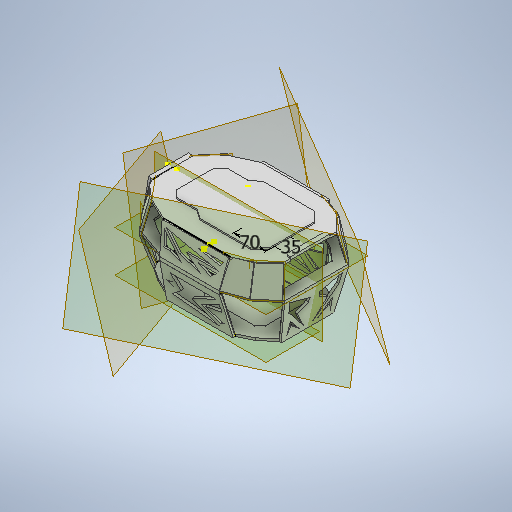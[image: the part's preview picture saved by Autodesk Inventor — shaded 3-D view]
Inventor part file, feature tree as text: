
AUTODESK INVENTOR PART (.ipt)
format: ipt  version: 2025.2 (Build 292293000, 293)  size: 6,125,568 bytes
history: native  units: mm
features: sketch x47, extrude x37, other x23, plane x17, loft x11, mirror x2, chamfer x2
ambient origin geometry x8: Origin, YZ Plane, XZ Plane, XY Plane, X Axis, Y Axis, Z Axis, Center Point
bodies: Body1 (feature_tree)
feature tree (139):
  extrude  "Extrusion2"  Depth=45.0mm
  extrude  "Extrusion3"  Depth=40.0mm
  plane  "Work Plane3"
  extrude  "Extrusion4"  Depth=145.0mm
  extrude  "Extrusion5"  Depth=55.0mm
  plane  "Work Plane4"
  extrude  "Extrusion6"  Depth=40.0mm
  sketch  "Sketch8"  dims[d17=165.0deg d18=15.0mm]
  sketch  "Sketch9"  dims[d20=10.0mm d21=40.0mm]
  sketch  "Sketch10"  dims[d22=5.0mm d23=5.0mm]
  loft  "Loft1"
  loft  "Loft2"
  extrude  "Extrusion7"  Depth=5.0mm
  extrude  "Extrusion8"  TaperAngle=90.0deg  [1 undecoded]
  extrude  "Extrusion9"  Depth=30.0mm
  sketch  "Sketch14"  dims[d30=45.0mm d31=20.0mm]
  sketch  "Sketch15"  dims[d32=45.0deg d39=5.0mm d40=0.0mm]
  sketch  "Sketch16"  dims[d41=3.0mm d42=3.0mm d43=0.0mm d44=0.0mm d45=150.0mm]
  loft  "Loft3"
  loft  "Loft4"
  loft  "Loft5"
  extrude  "Extrusion10"  Depth=150.0mm
  extrude  "Extrusion11"  Depth=10.0mm
  extrude  "Extrusion12"  Depth=10.0mm
  extrude  "Extrusion13"  Depth=10.0mm
  extrude  "Extrusion14"  Depth=10.0mm
  loft  "Loft7"
  loft  "Loft8"
  sketch  "Sketch22"  dims[d57=10.0mm d58=10.0mm]
  plane  "Work Plane5"
  extrude  "Extrusion15"  Depth=3.0mm TaperAngle=0.0deg
  plane  "Work Plane6"
  extrude  "Extrusion16"  Depth=10.0mm
  extrude  "Extrusion17"  Depth=50.0mm
  plane  "Work Plane7"
  extrude  "Extrusion18"  Depth=50.0mm
  sketch  "Sketch28"  dims[d71=27.925268mm d72=10.0mm]
  extrude  "Extrusion19"  Depth=10.0mm
  extrude  "Extrusion20"  Depth=60.0mm
  extrude  "Extrusion21"  Depth=5.0mm TaperAngle=0.0deg
  extrude  "Extrusion22"  TaperAngle=0.0deg  [1 undecoded]
  extrude  "Extrusion23"  TaperAngle=0.0deg  [1 undecoded]
  extrude  "Extrusion24"  Depth=4.0mm TaperAngle=0.0deg
  extrude  "Extrusion25"  TaperAngle=0.0deg  [1 undecoded]
  extrude  "Extrusion26"  TaperAngle=0.0deg  [1 undecoded]
  extrude  "Extrusion27"  TaperAngle=0.0deg  [1 undecoded]
  plane  "Work Plane8"
  mirror  "Mirror1"
  loft  "Loft9"
  loft  "Loft10"
  loft  "Loft11"
  loft  "Loft12"
  plane  "Work Plane14"
  plane  "Work Plane15"
  extrude  "Extrusion28"  TaperAngle=0.0deg  [1 undecoded]
  extrude  "Extrusion29"  Depth=4.0mm TaperAngle=0.0deg
  plane  "Work Plane16"
  extrude  "Extrusion30"  Depth=4.0mm
  mirror  "Mirror2"
  extrude  "Extrusion31"  Depth=70.0mm
  sketch  "Sketch42"  dims[d126=4.0mm d127=0.0mm d128=4.0mm d129=0.0mm]
  extrude  "Extrusion32"  Depth=10.0mm
  extrude  "Extrusion33"  Depth=70.0mm
  extrude  "Extrusion34"  Depth=35.0mm
  extrude  "Extrusion35"  Depth=23.0mm TaperAngle=0.0deg
  chamfer  "Chamfer1"  Distance=17.5mm
  extrude  "Extrusion36"  Depth=25.0mm
  chamfer  "Chamfer2"  Distance=30.0mm
  sketch  "Sketch48"  dims[d142=90.0deg d143=23.0mm d144=0.0mm]
  extrude  "Extrusion37"  TaperAngle=15.0deg  [1 undecoded]
  extrude  "Extrusion38"  TaperAngle=90.0deg  [1 undecoded]
  sketch  "Sketch1"  dims[d6=115.0mm d8=45.0mm]
  other  "Image1"
  sketch  "Sketch3"  dims[d9=45.0deg d10=40.0mm]
  sketch  "Sketch4"  dims[d11=27.925268mm d12=145.0mm]
  sketch  "Sketch5"  dims[d13=27.052603mm d14=55.0mm]
  sketch  "Sketch6"  dims[d15=27.052603mm d16=40.0mm]
  other  "Edges1"
  other  "Edges2"
  other  "Edges3"
  other  "Edges4"
  sketch  "Sketch11"  dims[d24=40.0mm d25=90.0deg]
  sketch  "Sketch12"  dims[d26=30.0mm d27=110.0mm]
  sketch  "Sketch13"  dims[d28=25.0mm d29=25.307274mm]
  other  "Edges5"
  other  "Edges6"
  other  "Edges7"
  other  "Edges8"
  other  "Edges9"
  other  "Edges10"
  sketch  "Sketch17"  dims[d46=10.0mm d48=10.0mm]
  sketch  "Sketch18"  dims[d49=10.0mm d50=22.68928mm]
  sketch  "Sketch19"  dims[d51=10.0mm d52=10.0mm]
  sketch  "Sketch20"  dims[d53=10.0mm d54=10.0mm]
  sketch  "Sketch21"  dims[d55=10.0mm d56=10.0mm]
  other  "Edges13"
  other  "Edges14"
  other  "Edges15"
  other  "Edges16"
  sketch  "Sketch23"  dims[d59=5.0mm d60=0.0mm d61=3.0mm d62=3.0mm d63=0.0mm d64=0.0mm]
  sketch  "Sketch24"  dims[d65=-90.0mm d66=10.0mm]
  sketch  "Sketch25"  dims[d67=70.0mm d68=50.0mm]
  sketch  "Sketch26"  dims[d69=22.68928mm d70=50.0mm]
  sketch  "Sketch29"  dims[d73=50.0mm d74=60.0mm]
  sketch  "Sketch30"  dims[d75=70.0mm d76=5.0mm d77=0.0mm]
  sketch  "Sketch31"  dims[d78=0.0mm d79=90.0deg d80=0.0mm d81=90.0deg]
  sketch  "Sketch32"  dims[d82=0.0mm d83=90.0deg d84=0.0mm d85=90.0deg]
  sketch  "Sketch33"  dims[d86=4.0mm d87=0.0mm d88=4.0mm d89=0.0mm]
  sketch  "Sketch34"  dims[d90=4.0mm d91=0.0mm d92=0.0mm d93=90.0deg]
  sketch  "Sketch35"  dims[d94=0.0mm d95=90.0deg d96=0.0mm d97=90.0deg]
  sketch  "Sketch36"  dims[d98=0.0mm d99=90.0deg d100=0.0mm d101=90.0deg]
  sketch  "Sketch37"  dims[d102=0.0mm d103=90.0deg d104=4.0mm d105=0.0mm]
  plane  "Work Plane9"
  plane  "Work Plane10"
  plane  "Work Plane11"
  plane  "Work Plane12"
  plane  "Work Plane13"
  other  "Edges17"
  other  "Edges18"
  other  "Edges19"
  other  "Edges20"
  other  "Edges21"
  other  "Edges22"
  other  "Edges23"
  other  "Edges24"
  sketch  "Sketch38"  dims[d106=4.0mm d107=0.0mm d108=4.0mm d109=0.0mm]
  sketch  "Sketch39"  dims[d110=4.0mm d111=0.0mm d112=4.0mm d113=0.0mm]
  sketch  "Sketch40"  dims[d118=0.0mm d119=90.0deg d120=0.0mm d121=90.0deg]
  plane  "Work Plane17"
  plane  "Work Plane18"
  plane  "Work Plane19"
  sketch  "Sketch41"  dims[d122=0.0mm d123=90.0deg d124=0.0mm d125=90.0deg]
  sketch  "Sketch43"  dims[d130=4.0mm d131=0.0mm d132=92.689mm]
  sketch  "Sketch44"  dims[d133=4.0mm d134=0.0mm d135=70.0mm]
  sketch  "Sketch45"  dims[d136=35.0mm d137=10.0mm]
  sketch  "Sketch46"  dims[d138=50.0mm d139=70.0mm]
  sketch  "Sketch47"  dims[d140=50.0mm d141=35.0mm]
  sketch  "Sketch49"  dims[d145=70.0mm]
  sketch  "Sketch50"  dims[d146=3.0mm d147=17.5mm d148=0.0mm d149=25.0mm d150=30.0mm d151=15.0deg d152=90.0deg d153=5.0mm d154=20.0mm d155=90.0deg d156=4.363323mm d157=17.5mm d158=0.0mm d159=25.0mm d160=165.0deg d161=40.0mm d162=150.0deg d163=50.0mm d164=1.745329mm d165=40.0mm d166=5.0mm d167=40.0mm d168=30.543262mm d169=17.5mm d170=0.0mm d171=10.0mm d172=100.0mm d173=150.0deg d174=40.0mm d175=19.198622mm d176=100.0mm d177=70.0mm d178=30.0deg d179=100.0mm d180=10.0mm d181=10.0mm d182=10.0mm d183=4.363323mm d184=40.0mm d185=40.0mm d186=6.981317mm d187=20.0mm d188=24.43461mm d189=16.0mm d190=10.0mm d191=0.0mm d192=80.0mm d193=24.43461mm d194=120.0mm d195=30.0deg d196=40.0mm d197=30.0deg d198=50.0mm d199=10.0mm d200=50.0mm d201=55.0mm d202=1.745329mm d203=30.0mm d204=27.925268mm d205=40.0mm d206=5.0mm d207=30.0mm d208=30.0mm d209=17.453293mm d210=60.0mm d211=30.0mm d212=50.0mm d213=0.0mm d214=10.0mm d215=10.0mm d216=10.0mm d217=10.0mm d218=90.0deg d219=10.0mm d220=20.0mm d221=10.0mm d222=17.453293mm d223=25.0mm d224=22.68928mm d225=70.0mm d226=10.0mm d227=40.0mm d228=22.68928mm d229=20.0mm d230=75.0deg d231=50.0mm d232=0.0mm d233=5.0mm d234=0.0mm d235=5.0mm d236=0.0mm d238=0.0mm d239=90.0deg d240=0.0mm d241=90.0deg d242=0.0mm d243=90.0deg d244=0.0mm d245=90.0deg d246=0.0mm d247=90.0deg d248=0.0mm d249=90.0deg d250=0.0mm d251=90.0deg d252=0.0mm d253=90.0deg d254=3.0mm d255=0.0mm d256=3.0mm d257=0.0mm d258=3.0mm d259=0.0mm d260=30.0mm d261=50.0mm d262=90.0mm d263=30.0mm d264=5.0mm d265=0.0mm d266=20.0mm d267=100.0mm d268=20.0mm d269=100.0mm d270=30.0mm d271=40.0mm d272=30.0mm d273=5.0mm d274=5.0mm d275=0.0mm d276=0.0mm d277=10.0mm d278=10.0mm d279=30.0mm d280=0.0mm d281=20.0mm d282=20.0mm d283=20.0mm d284=90.0deg d285=10.0mm d286=0.0mm d287=20.0mm d288=100.0mm d289=0.0mm d290=10.0mm d291=10.0mm d292=10.0mm d293=0.0mm d294=6.0mm d295=2.0mm d296=45.0deg d297=20.0mm d298=13.0mm d299=20.0mm d300=13.0mm d301=20.0mm d302=13.0mm d303=20.0mm d304=13.0mm d305=20.0mm d306=0.0mm d307=20.0mm d308=2.0mm d309=45.0deg d310=140.0mm d311=10.0mm d312=23.0mm d313=0.0mm d314=50.0mm d315=0.0mm]
note: 9 required parameter values undecoded (feature->parameter linkage not recoverable at this tier; creation-order binding heuristic only, values carry confidence <= 0.55)
